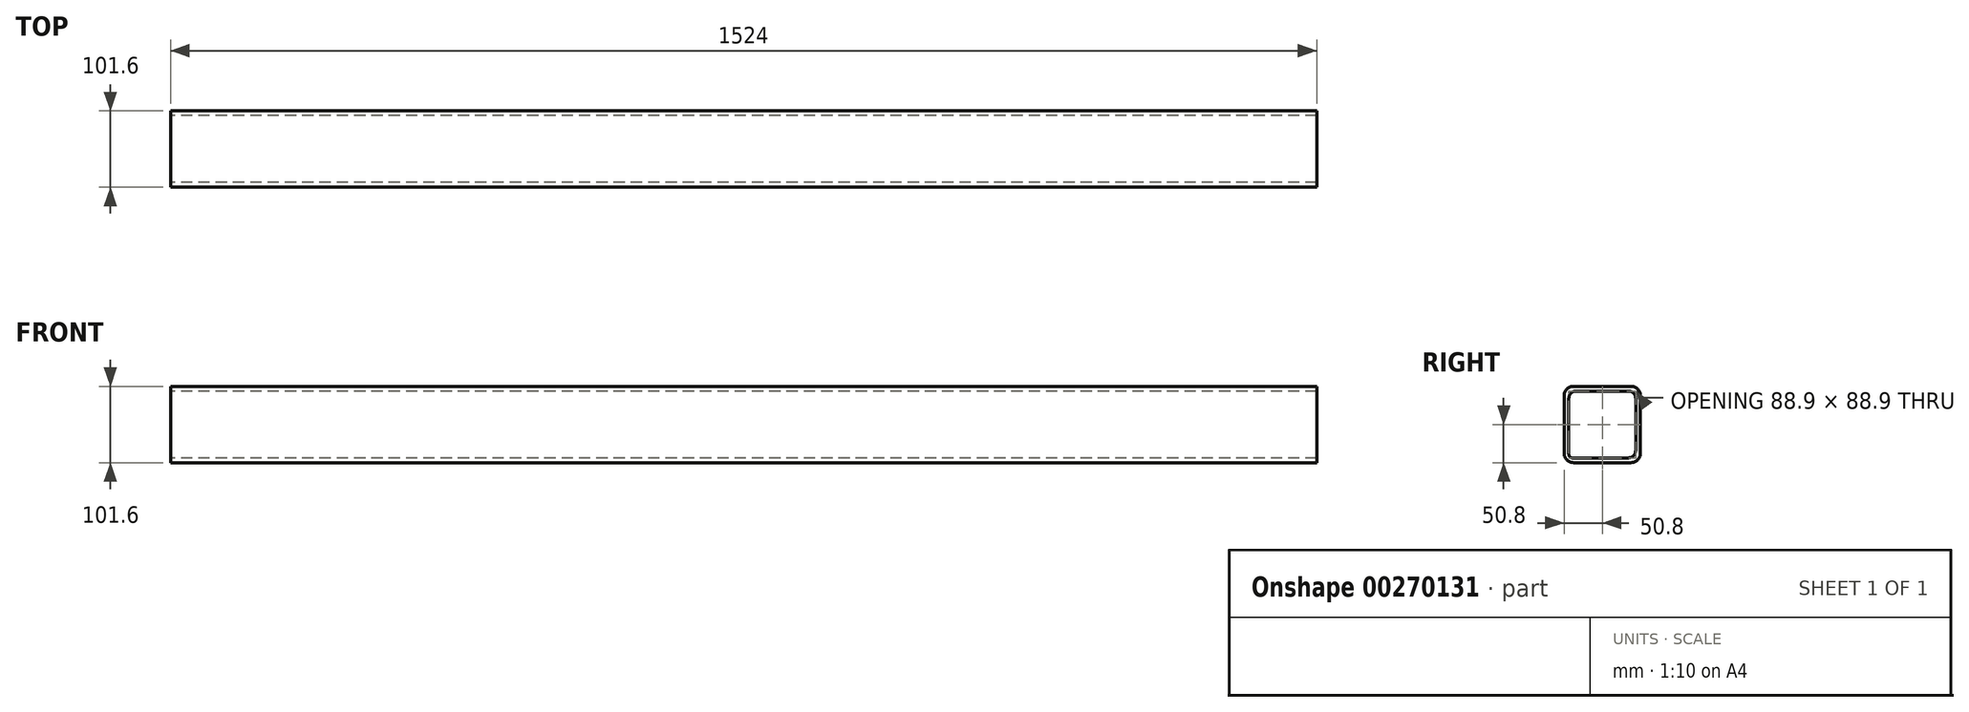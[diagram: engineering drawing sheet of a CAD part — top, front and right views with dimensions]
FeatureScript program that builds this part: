
annotation { "Feature Type Name" : "Feature", "Feature Type Description" : "" }
export const myFeature = defineFeature(function(context is Context, id is Id, definition is map)
    precondition{}
    {
        {
            var Q0;
            Q0=qCreatedBy(makeId("Right.planeOp"),FACE);
            var sketch = newSketch(context, id + "F0", { "sketchPlane" : qUnion([Q0])});
            skLineSegment(sketch, "E0.bottom", {"start": v(38.1, -50.8) * mm, "end": v(-38.1, -50.8) * mm});
            skLineSegment(sketch, "E0.top", {"start": v(38.1, 50.8) * mm, "end": v(-38.1, 50.8) * mm});
            skLineSegment(sketch, "E0.left", {"start": v(50.8, -38.1) * mm, "end": v(50.8, 38.1) * mm});
            skLineSegment(sketch, "E0.right", {"start": v(-50.8, -38.1) * mm, "end": v(-50.8, 38.1) * mm});
            skPoint(sketch, "E0.middle", {"position": v(0, 0) * mm});
            skPoint(sketch, "E1.visualSharp", {"position": v(-50.8, 50.8) * mm});
            skArc(sketch, "E1.filletArc", {"start": v(-38.1, 50.8) * mm, "mid": v(-47.08, 47.08) * mm, "end": v(-50.8, 38.1) * mm});
            skPoint(sketch, "E2.visualSharp", {"position": v(50.8, 50.8) * mm});
            skArc(sketch, "E2.filletArc", {"start": v(50.8, 38.1) * mm, "mid": v(47.08, 47.08) * mm, "end": v(38.1, 50.8) * mm});
            skPoint(sketch, "E3.visualSharp", {"position": v(50.8, -50.8) * mm});
            skArc(sketch, "E3.filletArc", {"start": v(38.1, -50.8) * mm, "mid": v(47.08, -47.08) * mm, "end": v(50.8, -38.1) * mm});
            skPoint(sketch, "E4.visualSharp", {"position": v(-50.8, -50.8) * mm});
            skArc(sketch, "E4.filletArc", {"start": v(-50.8, -38.1) * mm, "mid": v(-47.08, -47.08) * mm, "end": v(-38.1, -50.8) * mm});
            skLineSegment(sketch, "E5.bottom", {"start": v(34.6, -44.45) * mm, "end": v(-39.69, -44.45) * mm});
            skLineSegment(sketch, "E5.top", {"start": v(34.6, 44.45) * mm, "end": v(-34.6, 44.45) * mm});
            skLineSegment(sketch, "E5.left", {"start": v(44.45, -34.6) * mm, "end": v(44.45, 34.6) * mm});
            skLineSegment(sketch, "E5.right", {"start": v(-44.45, -39.69) * mm, "end": v(-44.45, 34.6) * mm});
            skPoint(sketch, "E6.visualSharp", {"position": v(-44.45, 44.45) * mm});
            skArc(sketch, "E6.filletArc", {"start": v(-34.6, 44.45) * mm, "mid": v(-41.57, 41.57) * mm, "end": v(-44.45, 34.6) * mm});
            skPoint(sketch, "E7.visualSharp", {"position": v(44.45, 44.45) * mm});
            skArc(sketch, "E7.filletArc", {"start": v(44.45, 34.6) * mm, "mid": v(41.57, 41.57) * mm, "end": v(34.6, 44.45) * mm});
            skPoint(sketch, "E8.visualSharp", {"position": v(-44.45, -44.45) * mm});
            skArc(sketch, "E8.filletArc", {"start": v(-44.45, -39.69) * mm, "mid": v(-43.06, -43.06) * mm, "end": v(-39.69, -44.45) * mm});
            skPoint(sketch, "E9.visualSharp", {"position": v(44.45, -44.45) * mm});
            skArc(sketch, "E9.filletArc", {"start": v(34.6, -44.45) * mm, "mid": v(41.57, -41.57) * mm, "end": v(44.45, -34.6) * mm});
            skSolve(sketch);
        }
        {
            var Q0;
            Q0=makeQuery(id+"F0.imprint","IMPRINT",FACE,{"disambiguationData":[TD([[makeQuery(id+"F0.imprint","IMPRINT",EDGE,{"derivedFrom":sQuery(id+"F0.wireOp",EDGE,"E0.bottom")}),-1.0]])]});
            extrude(context, id + "F1", {"entities" : qUnion([Q0]), "depth" : 1524 * mm});
        }
    });
